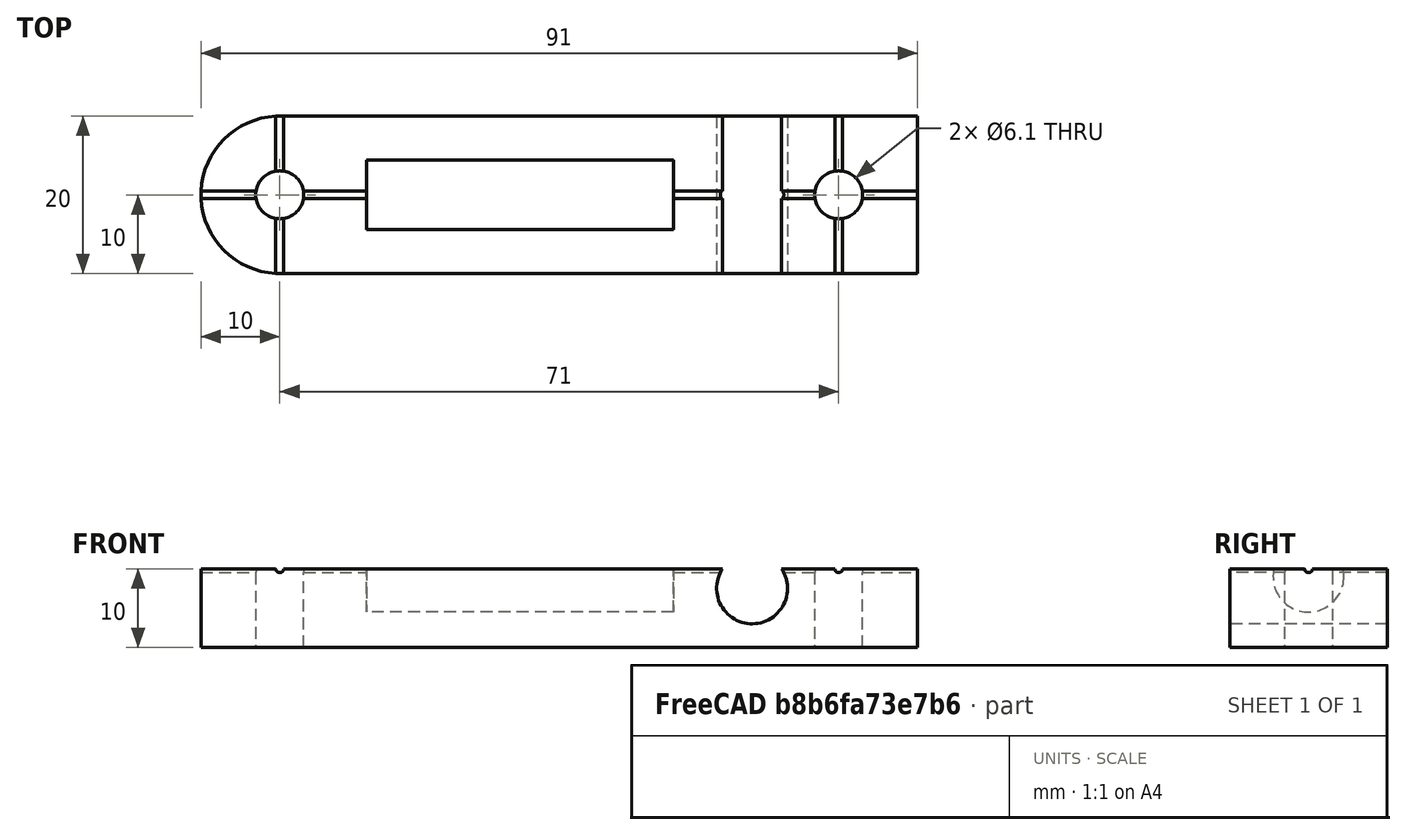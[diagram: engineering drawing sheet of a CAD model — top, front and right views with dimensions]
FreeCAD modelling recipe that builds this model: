
FCSTD DOCUMENT  (FreeCAD 1.0R39285 (Git))
Label: outlet-drillguide
License: All rights reserved
objects: Sketcher::SketchObject×5, PartDesign::Pocket×4, PartDesign::Pad×1, PartDesign::Body×1, Mesh::Feature×1
note: 26 computed .brp shape members not serialized (recipe doc carries the construction recipe); baked Part::Feature solids carry a one-line shape summary decoded from their .brp

FEATURE [Sketcher::SketchObject] Sketch
  ArcFitTolerance = 1e-06
  AttachmentSupport = -> [XY_Plane]
  FullyConstrained = true
  MakeInternals = false
  MapMode = 5
  sketch-geometry (7):
    g0: Circle CenterX=0 CenterY=0 CenterZ=0 NormalX=0 NormalY=0 NormalZ=1 AngleXU=0 Radius=3.05
    g1: Circle CenterX=71 CenterY=0 CenterZ=0 NormalX=0 NormalY=0 NormalZ=1 AngleXU=0 Radius=3.05
    g2: LineSegment StartX=9.396e-13 StartY=-10 StartZ=0 EndX=81 EndY=-10 EndZ=0
    g3: LineSegment StartX=81 StartY=-10 StartZ=0 EndX=81 EndY=10 EndZ=0
    g4: LineSegment StartX=81 StartY=10 StartZ=0 EndX=-1.85736e-11 EndY=10 EndZ=0
    g5: ArcOfCircle CenterX=0 CenterY=0 CenterZ=0 NormalX=0 NormalY=0 NormalZ=1 AngleXU=0 Radius=10 StartAngle=1.5708 EndAngle=3.14159
    g6: ArcOfCircle CenterX=0 CenterY=0 CenterZ=0 NormalX=0 NormalY=0 NormalZ=1 AngleXU=0 Radius=10 StartAngle=3.14159 EndAngle=4.71239
  constraints (21):
    c: Diameter(g0) = 6.1
    c: Diameter(g1) = 6.1
    c: DistanceX(g0,g1) = 71
    c: Distance(g1,g3) = 10
    c: Distance(g3,g-1) = 10
    c: Coincident(g2,g6)
    c: Coincident(g5,g4)
    c: Coincident(g3,g4)
    c: Coincident(g5,g6)
    c: Coincident(g6,g-1)
    c: PointOnObject(g5,g-1)
    c: PointOnObject(g2,g-2)
    c: PointOnObject(g4,g-2)
    c: PointOnObject(g1,g-1)
    c: Coincident(g2,g3)
    c: Coincident(g5,g6)
    c: Coincident(g0,g5)
    c: Parallel(g4,g2)
    c: Perpendicular(g-2,g2)
    c: Perpendicular(g-1,g3)
    c: DistanceX(g5,g0) = 10
FEATURE [PartDesign::Pad] Pad
  Direction = (0,0,1)
  Length = 10
  Length2 = 10
  Profile = -> Sketch
  ReferenceAxis = -> Sketch [N_Axis]
  Refine = true
  Suppressed = false
  Type = 0
FEATURE [Sketcher::SketchObject] Sketch001
  ArcFitTolerance = 1e-06
  AttachmentSupport = -> [Pad]
  FullyConstrained = true
  MakeInternals = false
  MapMode = 5
  Placement = pos=(-3.5e-15,-10,0) rot=(1,0,0;1.5708rad)
  sketch-geometry (1):
    g0: Circle CenterX=60 CenterY=7.5 CenterZ=0 NormalX=0 NormalY=0 NormalZ=1 AngleXU=0 Radius=4.5
  constraints (3):
    c: Diameter(g0) = 9
    c: Distance(g0,g-2) = 60
    c: Distance(g0,g-1) = 7.5
FEATURE [PartDesign::Pocket] Pocket
  BaseFeature = -> Pad
  Direction = (0,1,-2e-16)
  Length = 20
  Length2 = 5
  Profile = -> Sketch001
  ReferenceAxis = -> Sketch001 [N_Axis]
  Refine = true
  Suppressed = false
  Type = 0
FEATURE [Sketcher::SketchObject] Sketch003
  ArcFitTolerance = 1e-06
  AttachmentSupport = -> [Pocket]
  FullyConstrained = true
  MakeInternals = false
  MapMode = 5
  Placement = pos=(81,0,0) rot=(0.57735,0.57735,0.57735;2.0944rad)
  sketch-geometry (1):
    g0: Circle CenterX=0 CenterY=9 CenterZ=0 NormalX=0 NormalY=0 NormalZ=1 AngleXU=0 Radius=4.5
  constraints (3):
    c: PointOnObject(g0,g-2)
    c: Diameter(g0) = 9
    c: DistanceY(g-1,g0) = 9
FEATURE [PartDesign::Pocket] Pocket001
  BaseFeature = -> Pocket
  Direction = (-1,0,0)
  Length = 31
  Length2 = -70
  Profile = -> Sketch003
  ReferenceAxis = -> Sketch003 [N_Axis]
  Refine = true
  Suppressed = false
  Type = 4
FEATURE [Sketcher::SketchObject] Sketch004
  ArcFitTolerance = 1e-06
  AttachmentSupport = -> [Pocket001]
  FullyConstrained = true
  MakeInternals = false
  MapMode = 5
  Placement = pos=(-3.5e-15,-10,0) rot=(1,0,0;1.5708rad)
  sketch-geometry (2):
    g0: Circle CenterX=0 CenterY=10 CenterZ=0 NormalX=0 NormalY=0 NormalZ=1 AngleXU=0 Radius=0.5
    g1: Circle CenterX=71 CenterY=10 CenterZ=0 NormalX=0 NormalY=0 NormalZ=1 AngleXU=0 Radius=0.5
  constraints (6):
    c: Diameter(g0) = 1
    c: PointOnObject(g0,g-2)
    c: DistanceY(g-1,g0) = 10
    c: Diameter(g1) = 1
    c: Distance(g1,g-1) = 10
    c: Distance(g1,g-2) = 71
FEATURE [PartDesign::Pocket] Pocket002
  BaseFeature = -> Pocket001
  Direction = (0,1,-2e-16)
  Length = 5
  Length2 = 5
  Profile = -> Sketch004
  ReferenceAxis = -> Sketch004 [N_Axis]
  Refine = true
  Suppressed = false
  Type = 1
FEATURE [Sketcher::SketchObject] Sketch005
  ArcFitTolerance = 1e-06
  AttachmentSupport = -> [Pocket002]
  FullyConstrained = true
  MakeInternals = false
  MapMode = 5
  Placement = pos=(81,0,0) rot=(0.57735,0.57735,0.57735;2.0944rad)
  sketch-geometry (1):
    g0: Circle CenterX=0 CenterY=10 CenterZ=0 NormalX=0 NormalY=0 NormalZ=1 AngleXU=0 Radius=0.5
  constraints (3):
    c: Diameter(g0) = 1
    c: PointOnObject(g0,g-2)
    c: DistanceY(g-1,g0) = 10
FEATURE [PartDesign::Pocket] Pocket003
  BaseFeature = -> Pocket002
  Direction = (-1,0,0)
  Length = 5
  Length2 = 5
  Profile = -> Sketch005
  ReferenceAxis = -> Sketch005 [N_Axis]
  Refine = true
  Suppressed = false
  Type = 1
FEATURE [PartDesign::Body] Body
  AllowCompound = false
  Group = -> [Sketch,Pad,Sketch001,Pocket,Sketch003,Pocket001,Sketch004,Pocket002,Sketch005,Pocket003]
  Origin = -> Origin
  Tip = -> Pocket003
FEATURE [Mesh::Feature] Mesh  label="Body (Meshed)"
